# Revit family: Seat-Toilet_Transitional_SoftClose_SS114_TOTO
name_source: partatom
category: Plumbing Fixtures
revit_build: Autodesk Revit Architecture 2013 (Build: 20130531_2115(x64)
units: mm (PartAtom-declared; Revit-internal decimal feet)

## types (1)
- SS114
    04 CSI = 22 41 39
    95 CSI = 15416
    Assembly Code = D2090900
    Bowl Type = Elongated
    CAD Drawing URL = http://assets.totousa.com
    CW Connection = No
    Certification = IAPMO(cUPC), Intertek, State of Massachusetts, City of Los Angeles and others
    Code Compliance = UPC, IPC, NSPC, NPC Canada, and others
    Color Availability = #01 Cotton, #03 Bone, #11 Colonial White, #12 Sedona Beige, #51 Ebony
    Description = Elongated Softclose Seat
    Finish = Plastic - TOTO - 01 Cotton
    HW Connection = No
    Height = 2 5/8"
    Industry Standards = Meets and exceeds ASME A112.4.2, ASME A112.18.1/CSA B125.1, UL 1431, CSA C22.2 #68
    Length = 19 19/64"
    Manufacturer = TOTO USA, Inc.
    Manufacturer Fax = (770) 282-0002
    Material = Polypropylene
    Model = SS114
    Series = Soiree
    Shipping Weight = 6.60 lb
    Spec Sheet URL = http://assets.totousa.com
    Style = Transitional
    Subcategory = Seats
    Toto BIM Number = BM-00200
    URL = http://www.totousa.com
    Vent Connection = No
    Warranty = One Year Limited Warranty
    Warranty URL = http://www.totousa.com
    Waste Connection = No
    Width = 14 11/64"

## geometry (parser evidence)
native form markers: Blend x24, Sweep x2
no freeform markers — native parametric forms only
